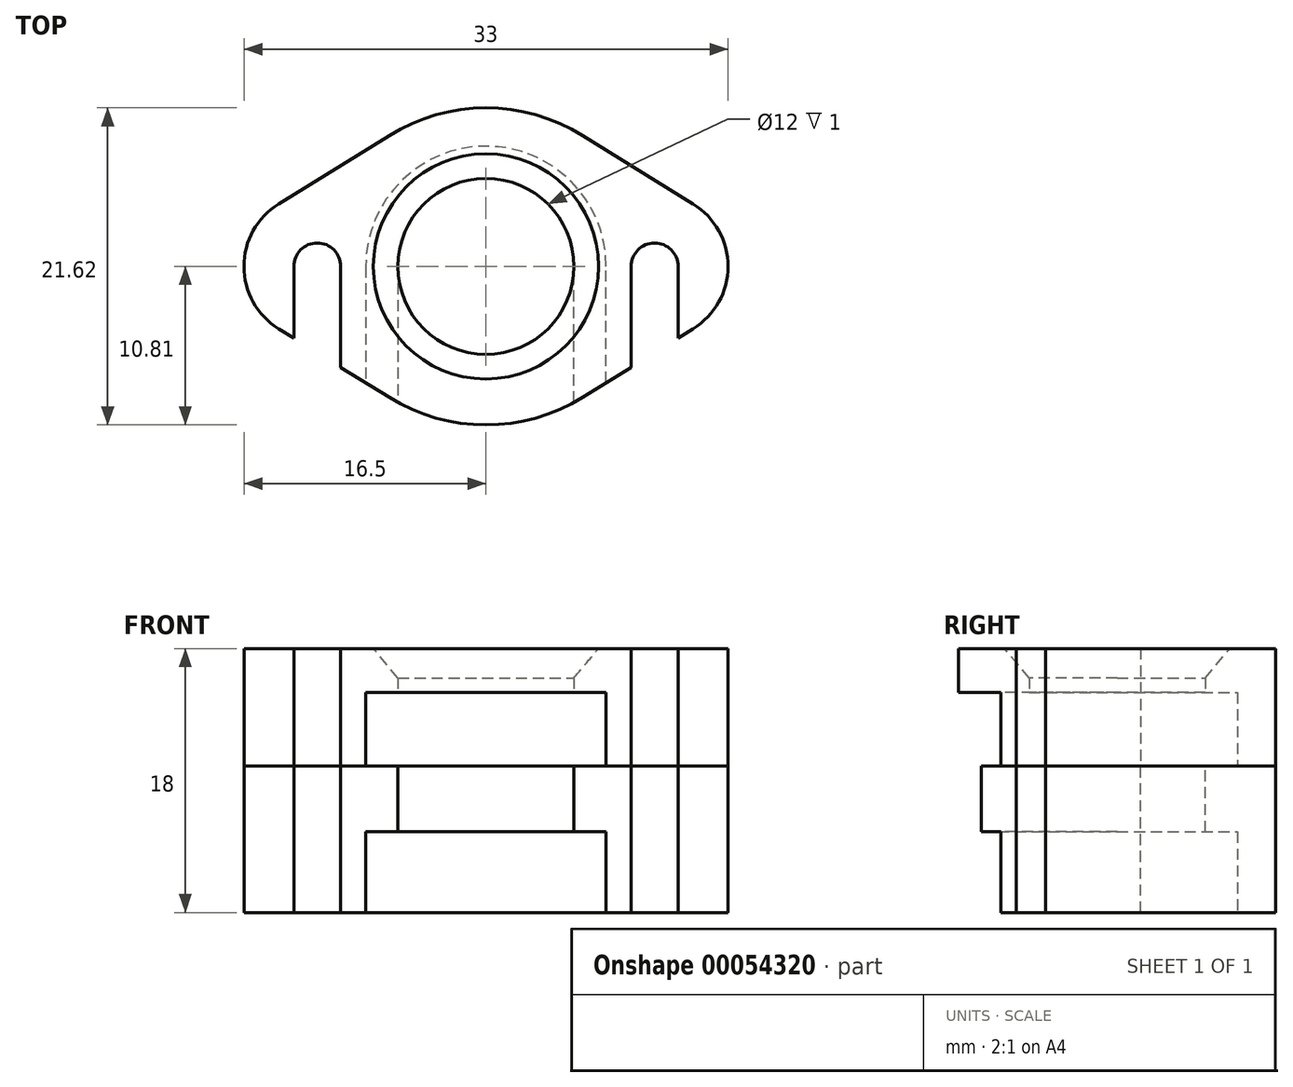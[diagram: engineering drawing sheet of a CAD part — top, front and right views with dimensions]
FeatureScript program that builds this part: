
annotation { "Feature Type Name" : "Feature", "Feature Type Description" : "" }
export const myFeature = defineFeature(function(context is Context, id is Id, definition is map)
    precondition{}
    {
        {
            var Q0;
            Q0=qCreatedBy(makeId("Top.planeOp"),FACE);
            var sketch = newSketch(context, id + "F0", { "sketchPlane" : qUnion([Q0])});
            skPoint(sketch, "E0", {"position": v(0, 0) * mm});
            skPoint(sketch, "E1", {"position": v(11.5, 0) * mm});
            skPoint(sketch, "E2", {"position": v(-11.5, 0) * mm});
            skCircle(sketch, "E3", {"center": v(0, 0) * mm, "radius": 8.2 * mm, "construction": true});
            skCircle(sketch, "E4", {"center": v(-11.5, 0) * mm, "radius": 1.6 * mm, "construction": true});
            skCircle(sketch, "E5", {"center": v(11.5, 0) * mm, "radius": 1.6 * mm, "construction": true});
            skLineSegment(sketch, "E6", {"start": v(-14.14, 4.25) * mm, "end": v(-6.6, 8.93) * mm, "construction": true});
            skLineSegment(sketch, "E7", {"start": v(6.6, 8.93) * mm, "end": v(14.14, 4.25) * mm, "construction": true});
            skLineSegment(sketch, "E8", {"start": v(14.14, -4.25) * mm, "end": v(6.6, -8.93) * mm, "construction": true});
            skLineSegment(sketch, "E9", {"start": v(-6.6, -8.93) * mm, "end": v(-14.14, -4.25) * mm, "construction": true});
            skArc(sketch, "E10", {"start": v(-14.14, 4.25) * mm, "mid": v(-16.5, 0) * mm, "end": v(-14.14, -4.25) * mm, "construction": true});
            skArc(sketch, "E11", {"start": v(6.6, 8.93) * mm, "mid": v(0, 10.81) * mm, "end": v(-6.6, 8.93) * mm, "construction": true});
            skArc(sketch, "E12", {"start": v(14.14, -4.25) * mm, "mid": v(16.5, 0) * mm, "end": v(14.14, 4.25) * mm, "construction": true});
            skArc(sketch, "E13", {"start": v(-6.6, -8.93) * mm, "mid": v(0, -10.81) * mm, "end": v(6.6, -8.93) * mm, "construction": true});
            skCircle(sketch, "E14", {"center": v(0, 0) * mm, "radius": 6 * mm, "construction": true});
            skSolve(sketch);
        }
        {
            var Q0;
            Q0=qCreatedBy(makeId("Top.planeOp"),FACE);
            var sketch = newSketch(context, id + "F1", { "sketchPlane" : qUnion([Q0])});
            skLineSegment(sketch, "E15.0", {"start": v(-14.14, 4.25) * mm, "end": v(-6.6, 8.93) * mm});
            skArc(sketch, "E15.1", {"start": v(6.6, 8.93) * mm, "mid": v(0, 10.81) * mm, "end": v(-6.6, 8.93) * mm});
            skArc(sketch, "E15.2", {"start": v(-14.14, 4.25) * mm, "mid": v(-16.5, 0) * mm, "end": v(-14.14, -4.25) * mm});
            skLineSegment(sketch, "E15.3", {"start": v(6.6, 8.93) * mm, "end": v(14.14, 4.25) * mm});
            skLineSegment(sketch, "E15.4", {"start": v(-6.6, -8.93) * mm, "end": v(-9.9, -6.88) * mm});
            skArc(sketch, "E15.5", {"start": v(-6.6, -8.93) * mm, "mid": v(0, -10.81) * mm, "end": v(6.6, -8.93) * mm});
            skLineSegment(sketch, "E15.6", {"start": v(14.14, -4.25) * mm, "end": v(13.1, -4.9) * mm});
            skArc(sketch, "E15.7", {"start": v(14.14, -4.25) * mm, "mid": v(16.5, 0) * mm, "end": v(14.14, 4.25) * mm});
            skCircle(sketch, "E16", {"center": v(0, 0) * mm, "radius": 6 * mm});
            skLineSegment(sketch, "E17", {"start": v(-13.1, -4.9) * mm, "end": v(-13.1, 0) * mm});
            skLineSegment(sketch, "E18", {"start": v(-9.9, -6.88) * mm, "end": v(-9.9, 0) * mm});
            skLineSegment(sketch, "E19", {"start": v(9.9, -6.88) * mm, "end": v(9.9, 0) * mm});
            skLineSegment(sketch, "E20", {"start": v(13.1, -4.9) * mm, "end": v(13.1, 0) * mm});
            skArc(sketch, "E21", {"start": v(13.1, 0) * mm, "mid": v(11.5, 1.6) * mm, "end": v(9.9, 0) * mm});
            skArc(sketch, "E22", {"start": v(-9.9, 0) * mm, "mid": v(-11.5, 1.6) * mm, "end": v(-13.1, 0) * mm});
            skLineSegment(sketch, "E23.trimOffspring", {"start": v(-13.1, -4.9) * mm, "end": v(-14.14, -4.25) * mm});
            skLineSegment(sketch, "E24.trimOffspring", {"start": v(9.9, -6.88) * mm, "end": v(6.6, -8.93) * mm});
            skSolve(sketch);
        }
        {
            var Q0;
            Q0 = qSketchRegion(id + "F1", true);
            extrude(context, id + "F2", {"entities" : qUnion([Q0]), "depth" : 8 * mm});
        }
        {
            var Q0;
            Q0=makeQuery(id+"F2.opExtrude","CAP_FACE",FACE,{"disambiguationData":[OSD([sQuery(id+"F1.wireOp",EDGE,"E15.0"),sQuery(id+"F1.wireOp",EDGE,"E15.1"),sQuery(id+"F1.wireOp",EDGE,"E15.2"),sQuery(id+"F1.wireOp",EDGE,"E15.3"),sQuery(id+"F1.wireOp",EDGE,"E15.4"),sQuery(id+"F1.wireOp",EDGE,"E15.5"),sQuery(id+"F1.wireOp",EDGE,"E15.6"),sQuery(id+"F1.wireOp",EDGE,"E15.7")])],"isStart":true});
            var sketch = newSketch(context, id + "F3", { "sketchPlane" : qUnion([Q0])});
            skLineSegment(sketch, "E25", {"start": v(-8.2, 7.93) * mm, "end": v(-8.2, 0) * mm});
            skLineSegment(sketch, "E26", {"start": v(8.2, 7.93) * mm, "end": v(8.2, 0) * mm});
            skArc(sketch, "E27", {"start": v(-8.2, 0) * mm, "mid": v(0, -8.2) * mm, "end": v(8.2, 0) * mm});
            skLineSegment(sketch, "E28", {"start": v(-8.2, 7.93) * mm, "end": v(-8.2, 12.46) * mm});
            skLineSegment(sketch, "E29", {"start": v(-8.2, 12.46) * mm, "end": v(8.2, 12.46) * mm});
            skLineSegment(sketch, "E30", {"start": v(8.2, 12.46) * mm, "end": v(8.2, 7.93) * mm});
            skSolve(sketch);
        }
        {
            var Q0;
            Q0 = qSketchRegion(id + "F3", true);
            extrude(context, id + "F4", {"entities" : qUnion([Q0]), "operationType" : NewBodyOperationType.REMOVE, "oppositeDirection" : true, "depth" : 5 * mm});
        }
        {
            var Q0;
            Q0=makeQuery(id+"F2.opExtrude","CAP_EDGE",EDGE,{"disambiguationData":[OSD([sQuery(id+"F1.wireOp",EDGE,"E16")])],"isStart":false});
            chamfer(context, id + "F5", {"entities" : qUnion([Q0]), "chamferType" : ChamferType.OFFSET_ANGLE, "width" : 2 * mm, "oppositeDirection" : false, "angle" : 40 * degree, "tangentPropagation" : true});
        }
        {
            var Q0;
            Q0=makeQuery(id+"F2.opExtrude","CAP_FACE",FACE,{"disambiguationData":[OSD([sQuery(id+"F1.wireOp",EDGE,"E15.0"),sQuery(id+"F1.wireOp",EDGE,"E15.1"),sQuery(id+"F1.wireOp",EDGE,"E15.2"),sQuery(id+"F1.wireOp",EDGE,"E15.3"),sQuery(id+"F1.wireOp",EDGE,"E15.4"),sQuery(id+"F1.wireOp",EDGE,"E15.5"),sQuery(id+"F1.wireOp",EDGE,"E15.6"),sQuery(id+"F1.wireOp",EDGE,"E15.7")])],"isStart":true});
            var sketch = newSketch(context, id + "F6", { "sketchPlane" : qUnion([Q0])});
            skArc(sketch, "E31.0", {"start": v(-6.6, 8.93) * mm, "mid": v(0, 10.81) * mm, "end": v(6.6, 8.93) * mm});
            skLineSegment(sketch, "E31.1", {"start": v(14.14, 4.25) * mm, "end": v(13.1, 4.9) * mm});
            skLineSegment(sketch, "E31.2", {"start": v(-6.6, 8.93) * mm, "end": v(-9.9, 6.88) * mm});
            skArc(sketch, "E31.3", {"start": v(14.14, 4.25) * mm, "mid": v(16.5, 0) * mm, "end": v(14.14, -4.25) * mm});
            skArc(sketch, "E31.4", {"start": v(-14.14, -4.25) * mm, "mid": v(-16.5, 0) * mm, "end": v(-14.14, 4.25) * mm});
            skLineSegment(sketch, "E31.5", {"start": v(-14.14, -4.25) * mm, "end": v(-6.6, -8.93) * mm});
            skArc(sketch, "E31.6", {"start": v(6.6, -8.93) * mm, "mid": v(0, -10.81) * mm, "end": v(-6.6, -8.93) * mm});
            skLineSegment(sketch, "E31.7", {"start": v(6.6, -8.93) * mm, "end": v(14.14, -4.25) * mm});
            skLineSegment(sketch, "E32", {"start": v(-13.1, 4.9) * mm, "end": v(-13.1, 0) * mm});
            skLineSegment(sketch, "E33", {"start": v(-9.9, 0) * mm, "end": v(-9.9, 6.88) * mm});
            skLineSegment(sketch, "E34", {"start": v(9.9, 0) * mm, "end": v(9.9, 6.88) * mm});
            skLineSegment(sketch, "E35", {"start": v(13.1, 0) * mm, "end": v(13.1, 4.9) * mm});
            skArc(sketch, "E36", {"start": v(9.9, 0) * mm, "mid": v(11.5, -1.6) * mm, "end": v(13.1, 0) * mm});
            skLineSegment(sketch, "E37.trimOffspring", {"start": v(9.9, 6.88) * mm, "end": v(6.6, 8.93) * mm});
            skLineSegment(sketch, "E38.trimOffspring", {"start": v(-13.1, 4.9) * mm, "end": v(-14.14, 4.25) * mm});
            skArc(sketch, "E39", {"start": v(-13.1, 0) * mm, "mid": v(-11.5, -1.6) * mm, "end": v(-9.9, 0) * mm});
            skSolve(sketch);
        }
        {
            var Q0;
            Q0 = qSketchRegion(id + "F6", true);
            extrude(context, id + "F7", {"entities" : qUnion([Q0]), "depth" : 10 * mm});
        }
        {
            var Q0;
            Q0=makeQuery(id+"F7.opExtrude","CAP_FACE",FACE,{"disambiguationData":[OSD([sQuery(id+"F6.wireOp",EDGE,"E31.0"),sQuery(id+"F6.wireOp",EDGE,"E31.1"),sQuery(id+"F6.wireOp",EDGE,"E31.2"),sQuery(id+"F6.wireOp",EDGE,"E31.3"),sQuery(id+"F6.wireOp",EDGE,"E31.4"),sQuery(id+"F6.wireOp",EDGE,"E31.5"),sQuery(id+"F6.wireOp",EDGE,"E31.6"),sQuery(id+"F6.wireOp",EDGE,"E31.7")])],"isStart":true});
            var sketch = newSketch(context, id + "F8", { "sketchPlane" : qUnion([Q0])});
            skArc(sketch, "E40", {"start": v(6, 0) * mm, "mid": v(0, 6) * mm, "end": v(-6, 0) * mm});
            skLineSegment(sketch, "E41", {"start": v(-6, 0) * mm, "end": v(-6, -13.52) * mm});
            skLineSegment(sketch, "E42", {"start": v(-6, -13.52) * mm, "end": v(6, -13.52) * mm});
            skLineSegment(sketch, "E43", {"start": v(6, -13.52) * mm, "end": v(6, 0) * mm});
            skSolve(sketch);
        }
        {
            var Q0;
            Q0 = qSketchRegion(id + "F8", true);
            extrude(context, id + "F9", {"entities" : qUnion([Q0]), "operationType" : NewBodyOperationType.REMOVE, "endBound" : BoundingType.UP_TO_NEXT, "oppositeDirection" : true, "depth" : 25 * mm});
        }
        {
            var Q0;
            Q0=makeQuery(id+"F7.opExtrude","CAP_FACE",FACE,{"disambiguationData":[OSD([sQuery(id+"F6.wireOp",EDGE,"E31.0"),sQuery(id+"F6.wireOp",EDGE,"E31.1"),sQuery(id+"F6.wireOp",EDGE,"E31.2"),sQuery(id+"F6.wireOp",EDGE,"E31.3"),sQuery(id+"F6.wireOp",EDGE,"E31.4"),sQuery(id+"F6.wireOp",EDGE,"E31.5"),sQuery(id+"F6.wireOp",EDGE,"E31.6"),sQuery(id+"F6.wireOp",EDGE,"E31.7"),sQuery(id+"F6.wireOp",EDGE,"E32"),sQuery(id+"F6.wireOp",EDGE,"E33"),sQuery(id+"F6.wireOp",EDGE,"E34"),sQuery(id+"F6.wireOp",EDGE,"E35"),sQuery(id+"F6.wireOp",EDGE,"E36"),sQuery(id+"F6.wireOp",EDGE,"E37.trimOffspring"),sQuery(id+"F6.wireOp",EDGE,"E38.trimOffspring"),sQuery(id+"F6.wireOp",EDGE,"E39")])],"isStart":false});
            var sketch = newSketch(context, id + "F10", { "sketchPlane" : qUnion([Q0])});
            skLineSegment(sketch, "E44", {"start": v(-8.2, 7.93) * mm, "end": v(-8.2, 0) * mm});
            skLineSegment(sketch, "E45", {"start": v(8.2, 7.93) * mm, "end": v(8.2, 0) * mm});
            skArc(sketch, "E46", {"start": v(-8.2, 0) * mm, "mid": v(0, -8.2) * mm, "end": v(8.2, 0) * mm});
            skLineSegment(sketch, "E47", {"start": v(-8.2, 7.93) * mm, "end": v(-8.2, 14.83) * mm});
            skLineSegment(sketch, "E48", {"start": v(-8.2, 14.83) * mm, "end": v(8.2, 14.83) * mm});
            skLineSegment(sketch, "E49", {"start": v(8.2, 14.83) * mm, "end": v(8.2, 7.93) * mm});
            skSolve(sketch);
        }
        {
            var Q0;
            Q0 = qSketchRegion(id + "F10", true);
            extrude(context, id + "F11", {"entities" : qUnion([Q0]), "operationType" : NewBodyOperationType.REMOVE, "oppositeDirection" : true, "depth" : 5.5 * mm});
        }
    });
